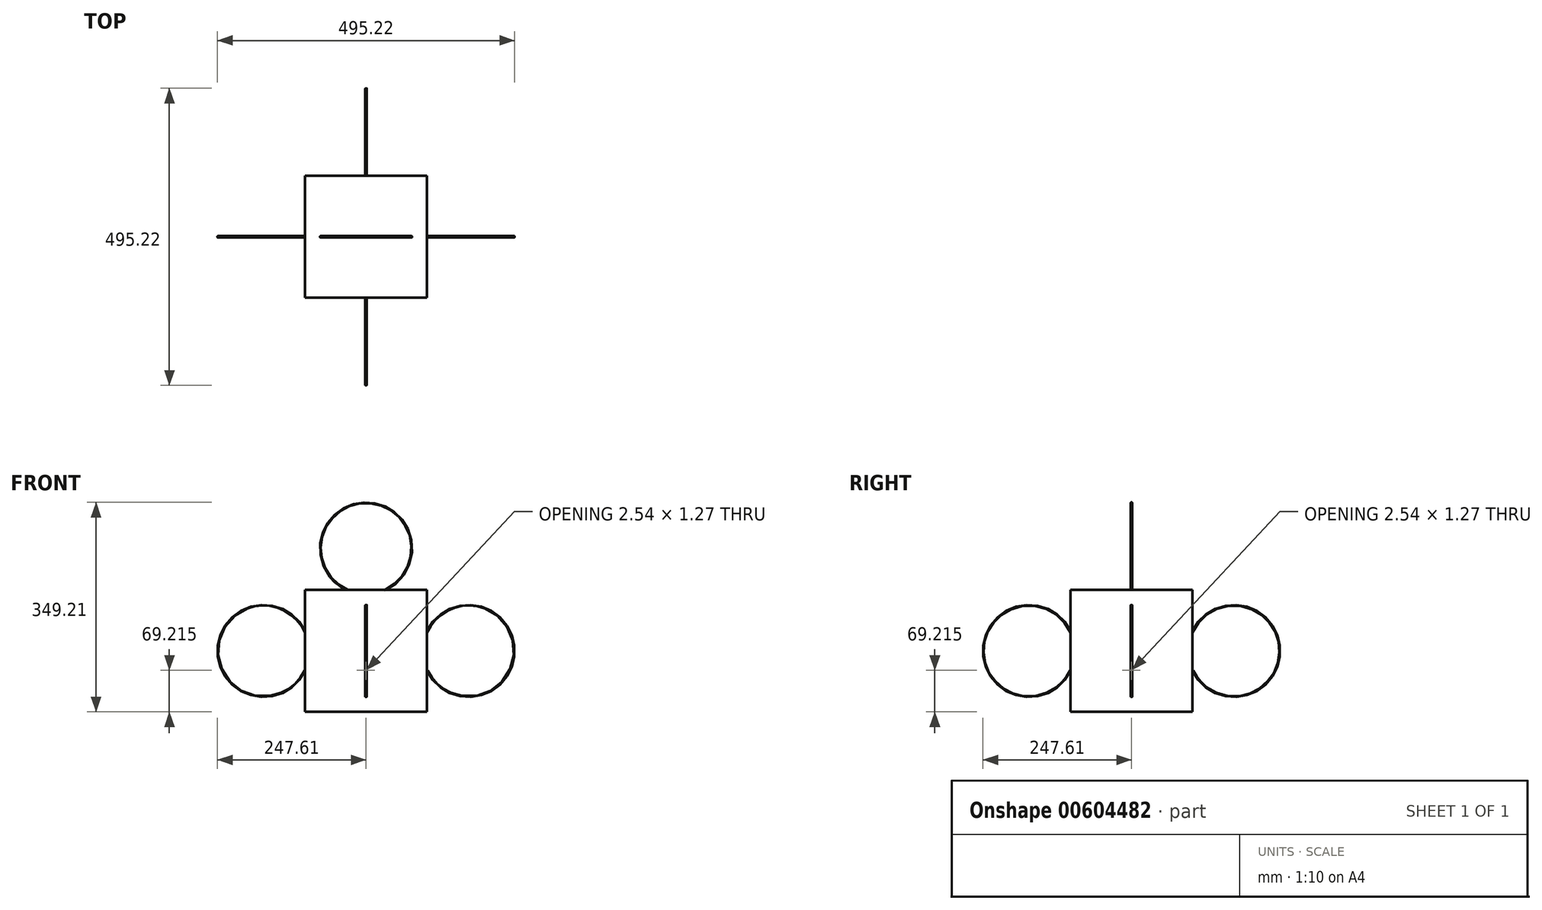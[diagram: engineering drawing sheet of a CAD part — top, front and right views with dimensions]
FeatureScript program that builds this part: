
annotation { "Feature Type Name" : "Feature", "Feature Type Description" : "" }
export const myFeature = defineFeature(function(context is Context, id is Id, definition is map)
    precondition{}
    {
        {
            var Q0;
            Q0=qCreatedBy(makeId("Top.planeOp"),FACE);
            var sketch = newSketch(context, id + "F0", { "sketchPlane" : qUnion([Q0])});
            skLineSegment(sketch, "E0.bottom", {"start": v(101.6, 101.6) * mm, "end": v(-101.6, 101.6) * mm});
            skLineSegment(sketch, "E0.top", {"start": v(101.6, -101.6) * mm, "end": v(-101.6, -101.6) * mm});
            skLineSegment(sketch, "E0.left", {"start": v(101.6, 101.6) * mm, "end": v(101.6, -101.6) * mm});
            skLineSegment(sketch, "E0.right", {"start": v(-101.6, 101.6) * mm, "end": v(-101.6, -101.6) * mm});
            skPoint(sketch, "E0.middle", {"position": v(0, 0) * mm});
            skSolve(sketch);
        }
        {
            var Q0;
            Q0 = qSketchRegion(id + "F0", true);
            extrude(context, id + "F1", {"entities" : qUnion([Q0]), "depth" : 203.2 * mm, "offsetDistance" : 25.4 * mm});
        }
        {
            var Q0;
            Q0=qCreatedBy(makeId("Right.planeOp"),FACE);
            var sketch = newSketch(context, id + "F2", { "sketchPlane" : qUnion([Q0])});
            skArc(sketch, "E1", {"start": v(101.6, 69.85) * mm, "mid": v(247.07, 101.6) * mm, "end": v(101.6, 133.35) * mm});
            skSolve(sketch);
        }
        {
            var Q0;
            Q0=makeQuery(id+"F1.opExtrude","SWEPT_FACE",FACE,{"disambiguationData":[OSD([sQuery(id+"F0.wireOp",EDGE,"E0.bottom")])]});
            var sketch = newSketch(context, id + "F3", { "sketchPlane" : qUnion([Q0])});
            skCircle(sketch, "E2", {"center": v(0, 133.35) * mm, "radius": 1.27 * mm});
            skSolve(sketch);
        }
        {
            var Q0;
            Q0=makeQuery(id+"F3.imprint","IMPRINT",FACE,{"disambiguationData":[TD([[makeQuery(id+"F3.imprint","IMPRINT",EDGE,{"derivedFrom":sQuery(id+"F3.wireOp",EDGE,"E2")}),1.0]])]});
            var Q1;
            Q1 = qConstructionFilter(qBodyType(qCreatedBy(id + "F2" ,EDGE), BodyType.WIRE), ConstructionObject.NO);
            sweep(context, id + "F4", {"operationType" : NewBodyOperationType.ADD, "profiles" : qUnion([Q0]), "path" : qUnion([Q1])});
        }
        {
            var Q0;
            Q0=qCreatedBy(makeId("Front.planeOp"),FACE);
            var sketch = newSketch(context, id + "F5", { "sketchPlane" : qUnion([Q0])});
            skLineSegment(sketch, "E3", {"start": v(0, 0) * mm, "end": v(0, 104.7) * mm});
            skSolve(sketch);
        }
        {
            var Q0;
            Q0=makeQuery(id+"F1.opExtrude","SWEPT_BODY",BODY,{"disambiguationData":[OSD([sQuery(id+"F0.wireOp",EDGE,"E0.bottom"),sQuery(id+"F0.wireOp",EDGE,"E0.top"),sQuery(id+"F0.wireOp",EDGE,"E0.left"),sQuery(id+"F0.wireOp",EDGE,"E0.right")])]});
            var Q1;
            Q1=sQuery(id+"F5.wireOp",EDGE,"E3");
            circularPattern(context, id + "F6", {"entities" : qUnion([Q0]), "axis" : qUnion([Q1]), "angle" : 360 * degree, "instanceCount" : 4, "equalSpace" : true});
        }
        {
            var Q0;
            Q0=qCreatedBy(makeId("Front.planeOp"),FACE);
            var sketch = newSketch(context, id + "F7", { "sketchPlane" : qUnion([Q0])});
            skArc(sketch, "E4", {"start": v(31.75, 203.2) * mm, "mid": v(0, 348.67) * mm, "end": v(-31.75, 203.2) * mm});
            skSolve(sketch);
        }
        {
            var Q0;
            Q0=makeQuery(id+"F1.opExtrude","CAP_FACE",FACE,{"disambiguationData":[OSD([sQuery(id+"F0.wireOp",EDGE,"E0.bottom"),sQuery(id+"F0.wireOp",EDGE,"E0.top"),sQuery(id+"F0.wireOp",EDGE,"E0.left"),sQuery(id+"F0.wireOp",EDGE,"E0.right")])],"isStart":false});
            var sketch = newSketch(context, id + "F8", { "sketchPlane" : qUnion([Q0])});
            skCircle(sketch, "E5", {"center": v(-31.75, 0) * mm, "radius": 1.27 * mm});
            skSolve(sketch);
        }
        {
            var Q0;
            Q0=makeQuery(id+"F8.imprint","IMPRINT",FACE,{"disambiguationData":[TD([[makeQuery(id+"F8.imprint","IMPRINT",EDGE,{"derivedFrom":sQuery(id+"F8.wireOp",EDGE,"E5")}),1.0]])]});
            var Q1;
            Q1=sQuery(id+"F7.wireOp",EDGE,"E4");
            sweep(context, id + "F9", {"profiles" : qUnion([Q0]), "path" : qUnion([Q1])});
        }
    });
